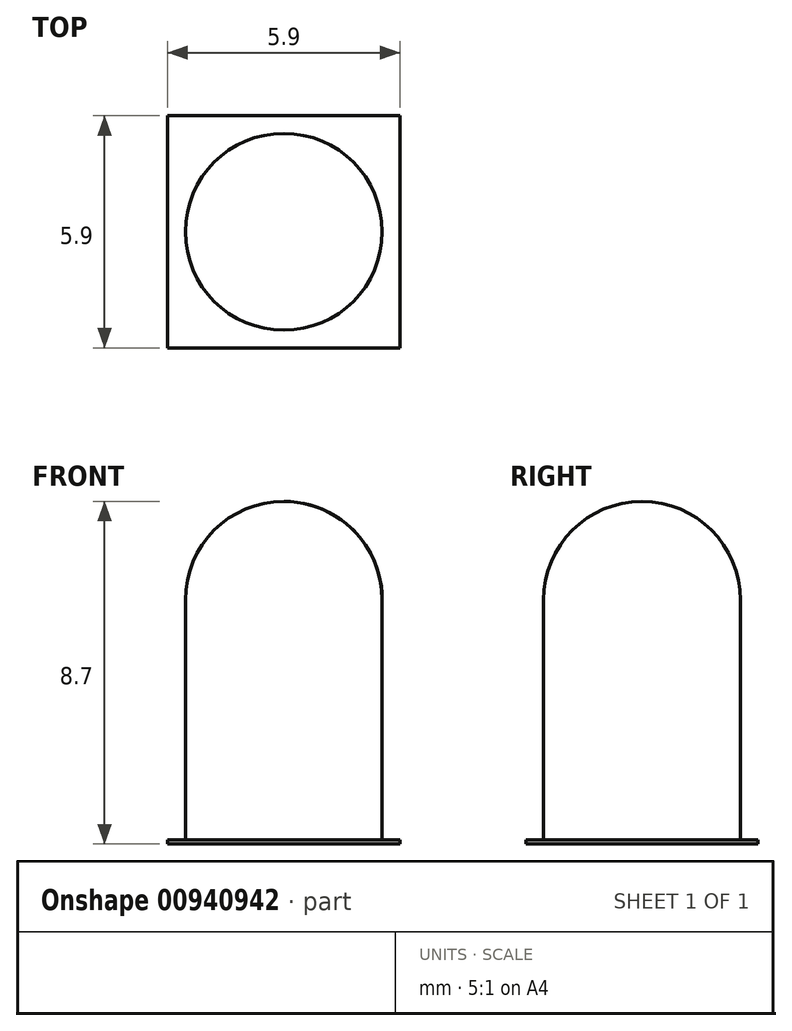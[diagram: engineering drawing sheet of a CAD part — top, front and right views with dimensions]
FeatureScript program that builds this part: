
annotation { "Feature Type Name" : "Feature", "Feature Type Description" : "" }
export const myFeature = defineFeature(function(context is Context, id is Id, definition is map)
    precondition{}
    {
        {
            var Q0;
            Q0=qCreatedBy(makeId("Top.planeOp"),FACE);
            var sketch = newSketch(context, id + "F0", { "sketchPlane" : qUnion([Q0])});
            skCircle(sketch, "E0", {"center": v(0, 0) * mm, "radius": 2.5 * mm});
            skLineSegment(sketch, "E1.bottom", {"start": v(2.95, 2.95) * mm, "end": v(-2.95, 2.95) * mm});
            skLineSegment(sketch, "E1.top", {"start": v(2.95, -2.95) * mm, "end": v(-2.95, -2.95) * mm});
            skLineSegment(sketch, "E1.left", {"start": v(2.95, 2.95) * mm, "end": v(2.95, -2.95) * mm});
            skLineSegment(sketch, "E1.right", {"start": v(-2.95, 2.95) * mm, "end": v(-2.95, -2.95) * mm});
            skSolve(sketch);
        }
        {
            var Q0;
            Q0 = qSketchRegion(id + "F0", true);
            extrude(context, id + "F1", {"entities" : qUnion([Q0]), "depth" : 0.1 * mm, "offsetDistance" : 25 * mm});
        }
        {
            var Q0;
            Q0=makeQuery(id+"F0.imprint","IMPRINT",FACE,{"disambiguationData":[TD([[makeQuery(id+"F0.imprint","IMPRINT",EDGE,{"derivedFrom":sQuery(id+"F0.wireOp",EDGE,"E0")}),1.0]])]});
            extrude(context, id + "F2", {"entities" : qUnion([Q0]), "operationType" : NewBodyOperationType.ADD, "depth" : 8.7 * mm, "offsetDistance" : 25 * mm});
        }
        {
            var Q0;
            Q0=makeQuery(id+"F2.opExtrude","CAP_EDGE",EDGE,{"disambiguationData":[OSD([sQuery(id+"F0.wireOp",EDGE,"E0")])],"isStart":false});
            fillet(context, id + "F3", {"entities" : qUnion([Q0]), "radius" : 2.5 * mm, "tangentPropagation" : true, "allowEdgeOverflow" : false});
        }
    });
